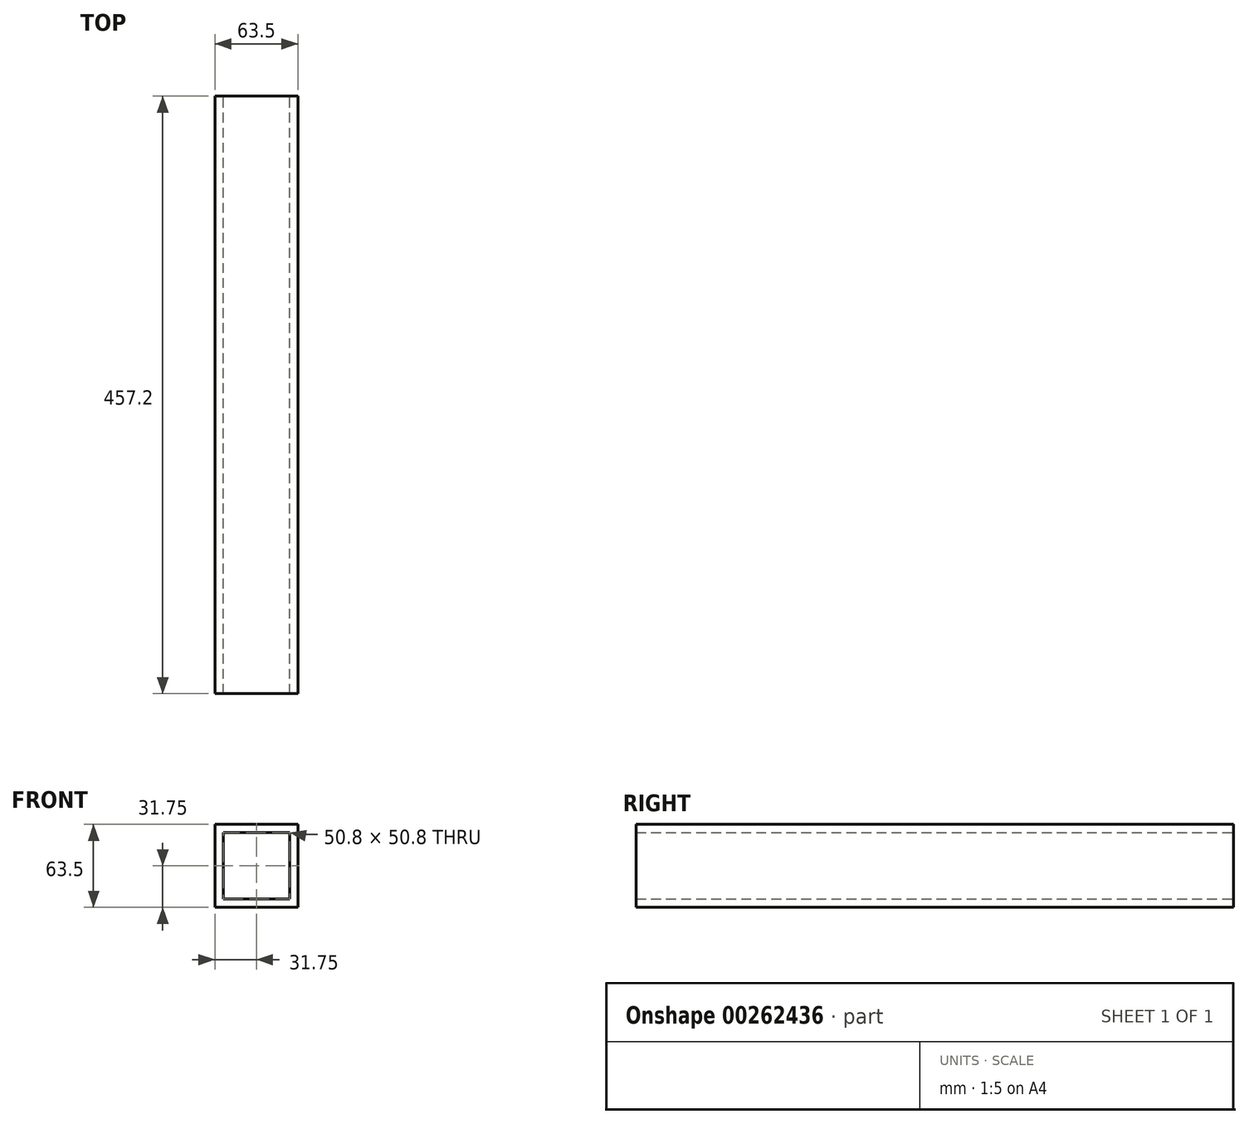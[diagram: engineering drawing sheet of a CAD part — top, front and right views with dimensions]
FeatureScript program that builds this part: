
annotation { "Feature Type Name" : "Feature", "Feature Type Description" : "" }
export const myFeature = defineFeature(function(context is Context, id is Id, definition is map)
    precondition{}
    {
        {
            var Q0;
            Q0=qCreatedBy(makeId("Front.planeOp"),FACE);
            var sketch = newSketch(context, id + "F0", { "sketchPlane" : qUnion([Q0])});
            skLineSegment(sketch, "E0.bottom", {"start": v(25.4, 25.4) * mm, "end": v(-25.4, 25.4) * mm});
            skLineSegment(sketch, "E0.top", {"start": v(25.4, -25.4) * mm, "end": v(-25.4, -25.4) * mm});
            skLineSegment(sketch, "E0.left", {"start": v(25.4, 25.4) * mm, "end": v(25.4, -25.4) * mm});
            skLineSegment(sketch, "E0.right", {"start": v(-25.4, 25.4) * mm, "end": v(-25.4, -25.4) * mm});
            skPoint(sketch, "E0.middle", {"position": v(0, 0) * mm});
            skLineSegment(sketch, "E1.bottom", {"start": v(31.75, 31.75) * mm, "end": v(-31.75, 31.75) * mm});
            skLineSegment(sketch, "E1.top", {"start": v(31.75, -31.75) * mm, "end": v(-31.75, -31.75) * mm});
            skLineSegment(sketch, "E1.left", {"start": v(31.75, 31.75) * mm, "end": v(31.75, -31.75) * mm});
            skLineSegment(sketch, "E1.right", {"start": v(-31.75, 31.75) * mm, "end": v(-31.75, -31.75) * mm});
            skSolve(sketch);
        }
        {
            var Q0;
            Q0 = qSketchRegion(id + "F0", true);
            extrude(context, id + "F1", {"entities" : qUnion([Q0]), "depth" : 457.2 * mm});
        }
    });
